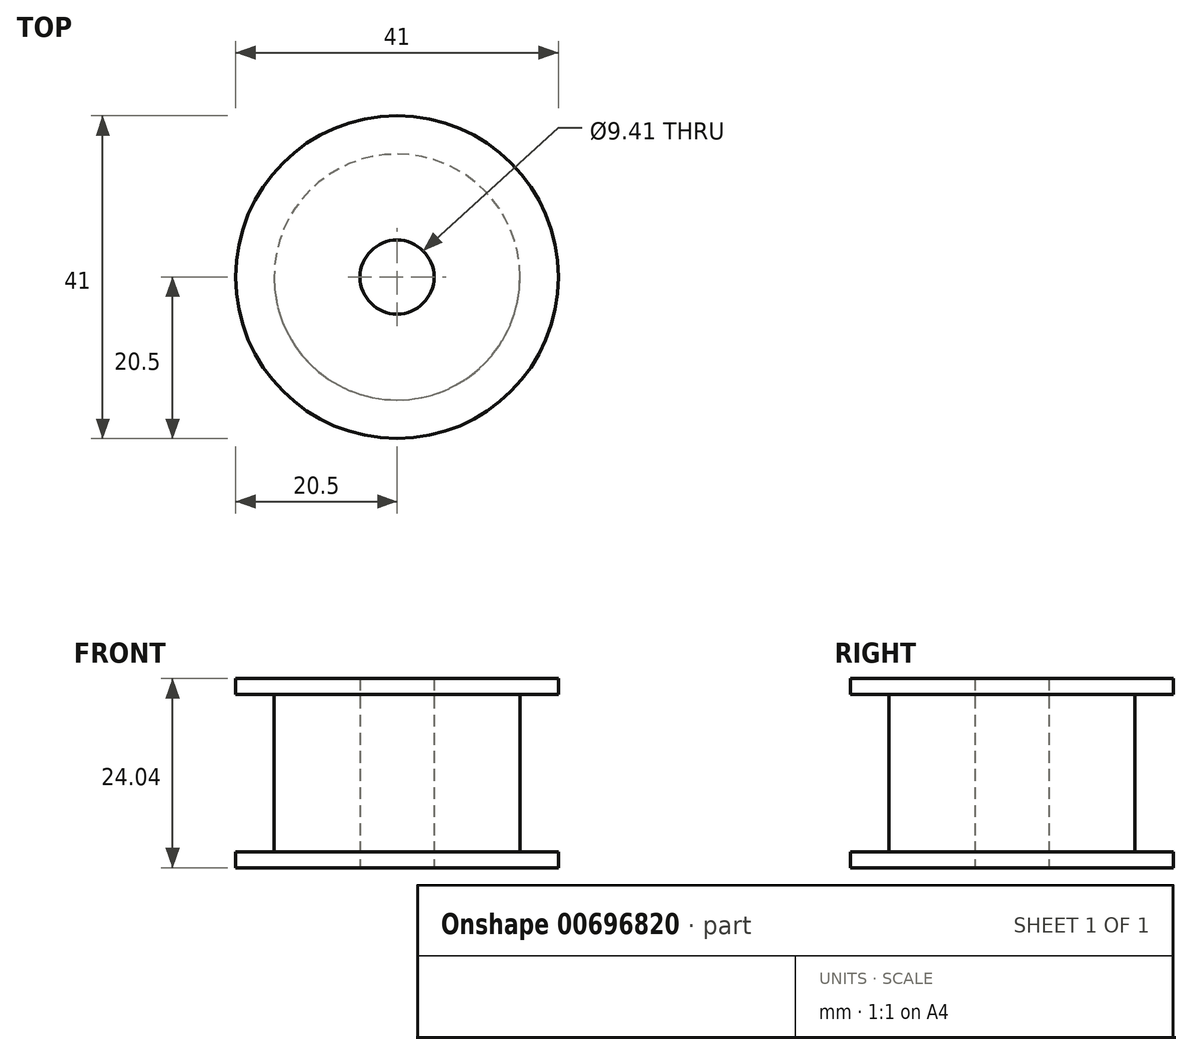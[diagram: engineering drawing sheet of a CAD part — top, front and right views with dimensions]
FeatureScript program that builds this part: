
annotation { "Feature Type Name" : "Feature", "Feature Type Description" : "" }
export const myFeature = defineFeature(function(context is Context, id is Id, definition is map)
    precondition{}
    {
        {
            var Q0;
            Q0=qCreatedBy(makeId("Top.planeOp"),FACE);
            var sketch = newSketch(context, id + "F0", { "sketchPlane" : qUnion([Q0])});
            skCircle(sketch, "E0", {"center": v(0, 0) * mm, "radius": 15.62 * mm});
            skCircle(sketch, "E1", {"center": v(0, 0) * mm, "radius": 5.71 * mm});
            skSolve(sketch);
        }
        {
            var Q0;
            Q0 = qSketchRegion(id + "F0", true);
            extrude(context, id + "F1", {"entities" : qUnion([Q0]), "depth" : 20 * mm, "offsetDistance" : 25 * mm});
        }
        {
            var Q0;
            Q0=makeQuery(id+"F1.opExtrude","CAP_FACE",FACE,{"disambiguationData":[OSD([sQuery(id+"F0.wireOp",EDGE,"E0"),sQuery(id+"F0.wireOp",EDGE,"E1")])],"isStart":false});
            var sketch = newSketch(context, id + "F2", { "sketchPlane" : qUnion([Q0])});
            skCircle(sketch, "E2", {"center": v(0, 0) * mm, "radius": 5.71 * mm});
            skCircle(sketch, "E3", {"center": v(0, 0) * mm, "radius": 4.7 * mm});
            skSolve(sketch);
        }
        {
            var Q0;
            Q0=makeQuery(id+"F2.imprint","IMPRINT",FACE,{"disambiguationData":[TD([[makeQuery(id+"F2.imprint","IMPRINT",EDGE,{"derivedFrom":sQuery(id+"F2.wireOp",EDGE,"E2")}),1.0]])]});
            extrude(context, id + "F3", {"entities" : qUnion([Q0]), "operationType" : NewBodyOperationType.ADD, "depth" : 2.02 * mm, "offsetDistance" : 25 * mm, "hasSecondDirection" : true, "secondDirectionOppositeDirection" : true, "secondDirectionDepth" : 22.02 * mm});
        }
        {
            var Q0;
            Q0=makeQuery(id+"F1.opExtrude","CAP_FACE",FACE,{"disambiguationData":[OSD([sQuery(id+"F0.wireOp",EDGE,"E0"),sQuery(id+"F0.wireOp",EDGE,"E1")])],"isStart":false});
            var sketch = newSketch(context, id + "F4", { "sketchPlane" : qUnion([Q0])});
            skCircle(sketch, "E4", {"center": v(0, 0) * mm, "radius": 5.71 * mm});
            skCircle(sketch, "E5", {"center": v(0, 0) * mm, "radius": 20.5 * mm});
            skSolve(sketch);
        }
        {
            var Q0;
            Q0 = qSketchRegion(id + "F4", true);
            extrude(context, id + "F5", {"entities" : qUnion([Q0]), "operationType" : NewBodyOperationType.ADD, "depth" : 2.02 * mm, "offsetDistance" : 25 * mm});
        }
        {
            var Q0;
            Q0=makeQuery(id+"F1.opExtrude","CAP_FACE",FACE,{"disambiguationData":[OSD([sQuery(id+"F0.wireOp",EDGE,"E0"),sQuery(id+"F0.wireOp",EDGE,"E1")])],"isStart":true});
            var sketch = newSketch(context, id + "F6", { "sketchPlane" : qUnion([Q0])});
            skCircle(sketch, "E6", {"center": v(0, 0) * mm, "radius": 5.71 * mm});
            skCircle(sketch, "E7", {"center": v(0, 0) * mm, "radius": 20.5 * mm});
            skSolve(sketch);
        }
        {
            var Q0;
            Q0 = qSketchRegion(id + "F6", true);
            extrude(context, id + "F7", {"entities" : qUnion([Q0]), "operationType" : NewBodyOperationType.ADD, "depth" : 2.02 * mm, "offsetDistance" : 25 * mm});
        }
    });
